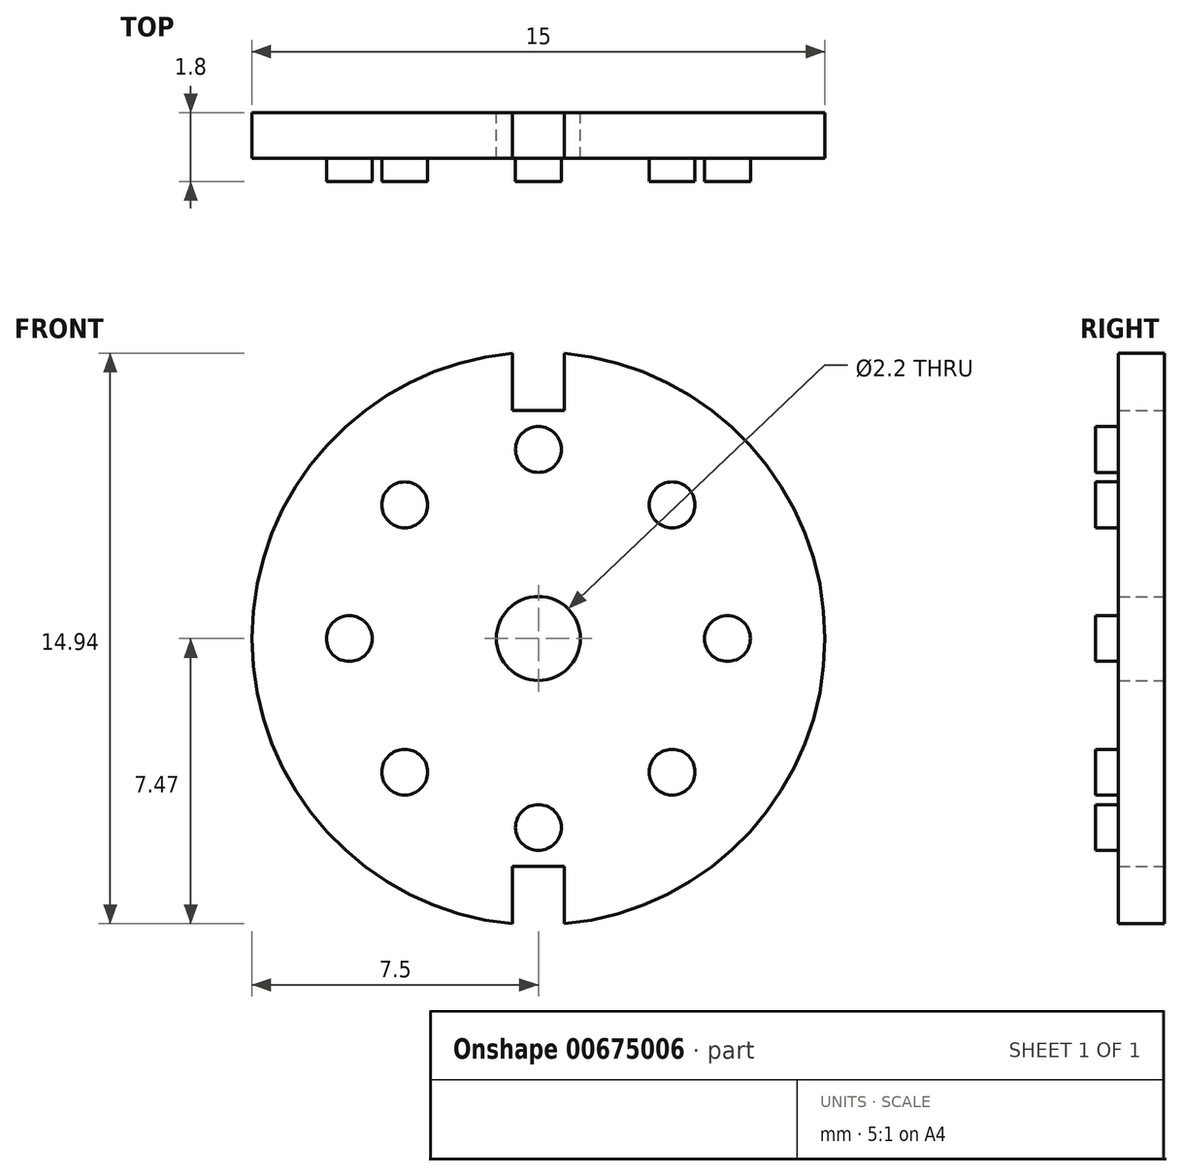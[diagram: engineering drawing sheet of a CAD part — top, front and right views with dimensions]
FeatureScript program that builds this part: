
annotation { "Feature Type Name" : "Feature", "Feature Type Description" : "" }
export const myFeature = defineFeature(function(context is Context, id is Id, definition is map)
    precondition{}
    {
        {
            assignVariable(context, id + "F0", {"name" : "Faktor", "anyValue" : 1.5});
        }
        {
            var Q0;
            Q0=qCreatedBy(makeId("Front.planeOp"),FACE);
            var sketch = newSketch(context, id + "F1", { "sketchPlane" : qUnion([Q0])});
            skArc(sketch, "E0", {"start": v(-0.68, 7.47) * mm, "mid": v(-7.5, 0) * mm, "end": v(-0.68, -7.47) * mm});
            skCircle(sketch, "E1", {"center": v(0, 0) * mm, "radius": 1.1 * mm});
            skLineSegment(sketch, "E2.top", {"start": v(-0.68, 5.97) * mm, "end": v(0.68, 5.97) * mm});
            skLineSegment(sketch, "E2.left", {"start": v(-0.68, 7.47) * mm, "end": v(-0.68, 5.97) * mm});
            skLineSegment(sketch, "E2.right", {"start": v(0.68, 7.47) * mm, "end": v(0.68, 5.97) * mm});
            skLineSegment(sketch, "E3.top", {"start": v(-0.67, -5.97) * mm, "end": v(0.67, -5.97) * mm});
            skLineSegment(sketch, "E3.left", {"start": v(-0.67, -7.47) * mm, "end": v(-0.67, -5.97) * mm});
            skLineSegment(sketch, "E3.right", {"start": v(0.67, -7.47) * mm, "end": v(0.67, -5.97) * mm});
            skArc(sketch, "E4.trimOffspring", {"start": v(0.67, -7.47) * mm, "mid": v(7.5, 0) * mm, "end": v(0.67, 7.47) * mm});
            skSolve(sketch);
        }
        {
            var Q0;
            Q0=qSketchRegion(id+"F1",true);
            extrude(context, id + "F2", {"entities" : qUnion([Q0]), "depth" : getVariable(context, 'Faktor') * 0.8 * mm, "offsetDistance" : 25 * mm});
        }
        {
            var Q0;
            Q0=makeQuery(id+"F2.opExtrude","CAP_FACE",FACE,{"disambiguationData":[OSD([sQuery(id+"F1.wireOp",EDGE,"E0")])],"isStart":false});
            var sketch = newSketch(context, id + "F3", { "sketchPlane" : qUnion([Q0])});
            skCircle(sketch, "E5", {"center": v(0, 4.95) * mm, "radius": 0.6 * mm});
            skSolve(sketch);
        }
        {
            var Q0;
            Q0=qSketchRegion(id+"F3",true);
            extrude(context, id + "F4", {"entities" : qUnion([Q0]), "depth" : getVariable(context, 'Faktor') * 0.4 * mm, "offsetDistance" : 25 * mm});
        }
        {
            var Q0;
            Q0=makeQuery(id+"F4.opExtrude","SWEPT_BODY",BODY,{"disambiguationData":[OSD([sQuery(id+"F3.wireOp",EDGE,"E5")])]});
            var Q1;
            Q1=makeQuery(id+"F2.opExtrude","CAP_EDGE",EDGE,{"disambiguationData":[OSD([sQuery(id+"F1.wireOp",EDGE,"E0")])],"isStart":false});
            circularPattern(context, id + "F5", {"entities" : qUnion([Q0]), "axis" : qUnion([Q1]), "angle" : 360 * degree, "instanceCount" : 8, "equalSpace" : true});
        }
    });
